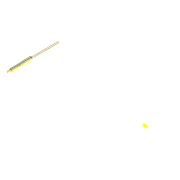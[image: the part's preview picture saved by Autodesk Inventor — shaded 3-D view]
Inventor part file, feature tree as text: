
AUTODESK INVENTOR PART (.ipt)
format: ipt  version: 2022 (Build 260153000, 153)  size: 129,024 bytes
history: native  units: mm
features: sketch x4, extrude x2, projected_geometry x2
ambient origin geometry x8: Origin, YZ Plane, XZ Plane, XY Plane, X Axis, Y Axis, Z Axis, Center Point
bodies: Solid1 (feature_tree)
feature tree (8):
  extrude  "Extrusion1"  Depth=8.0mm
  sketch  "Sketch2"  dims[d2=3.0mm d3=3.0mm]
  extrude  "Extrusion2"  Depth=3.0mm
  sketch  "Sketch4"  dims[d10=3.0mm d11=19.5mm d12=80.0mm d13=85.0mm d14=220.0mm d15=700.0mm d16=700.0mm d17=20.0mm d18=0.0mm]
  sketch  "Sketch1"  dims[d0=270.69mm d1=8.0mm]
  projected_geometry  "Projected Loop1"
  sketch  "Sketch3"  dims[d4=8.0mm d5=0.0mm]
  projected_geometry  "Projected Loop2"
